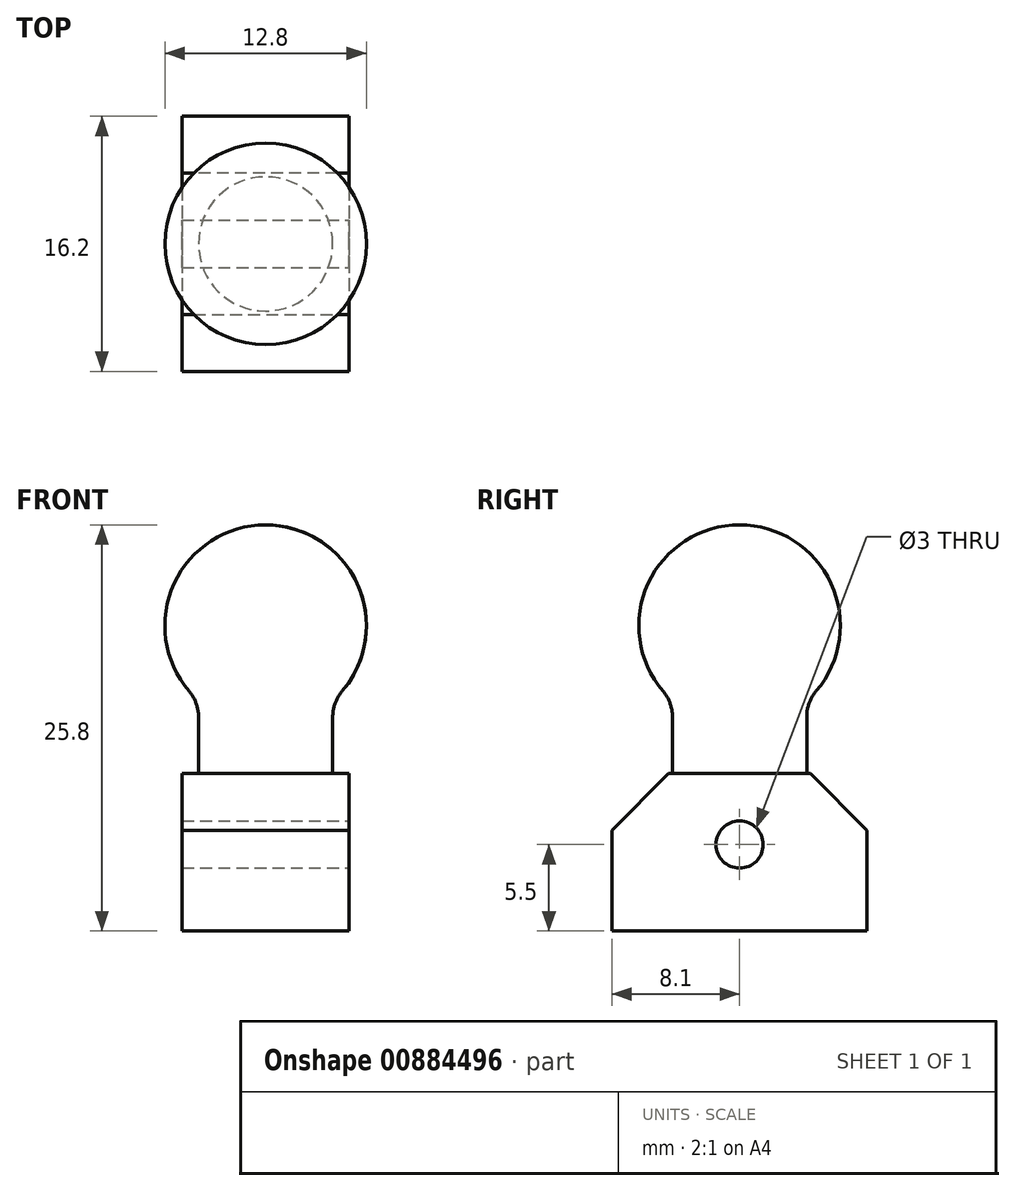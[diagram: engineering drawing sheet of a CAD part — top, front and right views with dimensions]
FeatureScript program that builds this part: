
annotation { "Feature Type Name" : "Feature", "Feature Type Description" : "" }
export const myFeature = defineFeature(function(context is Context, id is Id, definition is map)
    precondition{}
    {
        {
            var Q0;
            Q0=qCreatedBy(makeId("Front.planeOp"),FACE);
            var sketch = newSketch(context, id + "F0", { "sketchPlane" : qUnion([Q0])});
            skArc(sketch, "E0", {"start": v(4.26, 5.63) * mm, "mid": v(5.98, 12.68) * mm, "end": v(0, 16.8) * mm});
            skLineSegment(sketch, "E1", {"start": v(4.26, 5.63) * mm, "end": v(4.26, 0) * mm});
            skLineSegment(sketch, "E2", {"start": v(4.26, 0) * mm, "end": v(0, 0) * mm});
            skLineSegment(sketch, "E3", {"start": v(0, 0) * mm, "end": v(0, 16.8) * mm});
            skLineSegment(sketch, "E4", {"start": v(0, 16.8) * mm, "end": v(0, 44.7) * mm, "construction": true});
            skLineSegment(sketch, "E5", {"start": v(0, 8.4) * mm, "end": v(6.08, 8.4) * mm, "construction": true});
            skLineSegment(sketch, "E6", {"start": v(0, 10.4) * mm, "end": v(6.08, 8.4) * mm, "construction": true});
            skLineSegment(sketch, "E7", {"start": v(0, 10.4) * mm, "end": v(4.26, 5.63) * mm, "construction": true});
            skSolve(sketch);
        }
        {
            var Q0;
            Q0=makeQuery(id+"F0.imprint","IMPRINT",FACE,{"disambiguationData":[TD([[makeQuery(id+"F0.imprint","IMPRINT",EDGE,{"derivedFrom":sQuery(id+"F0.wireOp",EDGE,"E0")}),1.0]])]});
            var Q1;
            Q1=sQuery(id+"F0.wireOp",EDGE,"E4");
            revolve(context, id + "F1", {"surfaceOperationType" : NewSurfaceOperationType.NEW, "entities" : qUnion([Q0]), "axis" : qUnion([Q1]), "revolveType" : RevolveType.FULL});
        }
        {
            var Q0;
            Q0=qCreatedBy(makeId("Top.planeOp"),FACE);
            var sketch = newSketch(context, id + "F2", { "sketchPlane" : qUnion([Q0])});
            skLineSegment(sketch, "E8.bottom", {"start": v(5.3, 8.1) * mm, "end": v(-5.3, 8.1) * mm});
            skLineSegment(sketch, "E8.top", {"start": v(5.3, -8.1) * mm, "end": v(-5.3, -8.1) * mm});
            skLineSegment(sketch, "E8.left", {"start": v(5.3, 8.1) * mm, "end": v(5.3, -8.1) * mm});
            skLineSegment(sketch, "E8.right", {"start": v(-5.3, 8.1) * mm, "end": v(-5.3, -8.1) * mm});
            skPoint(sketch, "E8.middle", {"position": v(0, 0) * mm});
            skSolve(sketch);
        }
        {
            var Q0;
            Q0 = qSketchRegion(id + "F2", true);
            extrude(context, id + "F3", {"entities" : qUnion([Q0]), "operationType" : NewBodyOperationType.ADD, "depth" : 1 * mm, "offsetDistance" : 25 * mm, "hasSecondDirection" : true, "secondDirectionOppositeDirection" : true, "secondDirectionDepth" : 9 * mm});
        }
        {
            var Q0;
            Q0=makeQuery(id+"F3.opExtrude","SWEPT_FACE",FACE,{"disambiguationData":[OSD([sQuery(id+"F2.wireOp",EDGE,"E8.left")])]});
            var sketch = newSketch(context, id + "F4", { "sketchPlane" : qUnion([Q0])});
            skLineSegment(sketch, "E9", {"start": v(-8.1, -8) * mm, "end": v(8.1, -8) * mm, "construction": true});
            skCircle(sketch, "E10", {"center": v(0, -3.5) * mm, "radius": 1.5 * mm});
            skLineSegment(sketch, "E11", {"start": v(-8.1, -8) * mm, "end": v(8.1, 1) * mm, "construction": true});
            skSolve(sketch);
        }
        {
            var Q0;
            Q0 = qSketchRegion(id + "F4", true);
            extrude(context, id + "F5", {"entities" : qUnion([Q0]), "operationType" : NewBodyOperationType.REMOVE, "endBound" : BoundingType.UP_TO_NEXT, "oppositeDirection" : true, "depth" : 25 * mm, "offsetDistance" : 25 * mm});
        }
        {
            var Q0;
            Q0=makeQuery(id+"F3.opExtrude","CAP_EDGE",EDGE,{"disambiguationData":[OSD([sQuery(id+"F2.wireOp",EDGE,"E8.bottom")])],"isStart":false});
            var Q1;
            Q1=makeQuery(id+"F3.opExtrude","CAP_EDGE",EDGE,{"disambiguationData":[OSD([sQuery(id+"F2.wireOp",EDGE,"E8.top")])],"isStart":false});
            chamfer(context, id + "F6", {"entities" : qUnion([Q0, Q1]), "width" : 3.6 * mm, "tangentPropagation" : true});
        }
        {
            var Q0;
            Q0=makeQuery(id+"F1.opRevolve","SWEPT_EDGE",EDGE,{"disambiguationData":[OSD([sQuery(id+"F0.wireOp",EDGE,"E0"),sQuery(id+"F0.wireOp",EDGE,"E1")])]});
            fillet(context, id + "F7", {"entities" : qUnion([Q0]), "radius" : 2.5 * mm, "tangentPropagation" : true, "allowEdgeOverflow" : false});
        }
    });
